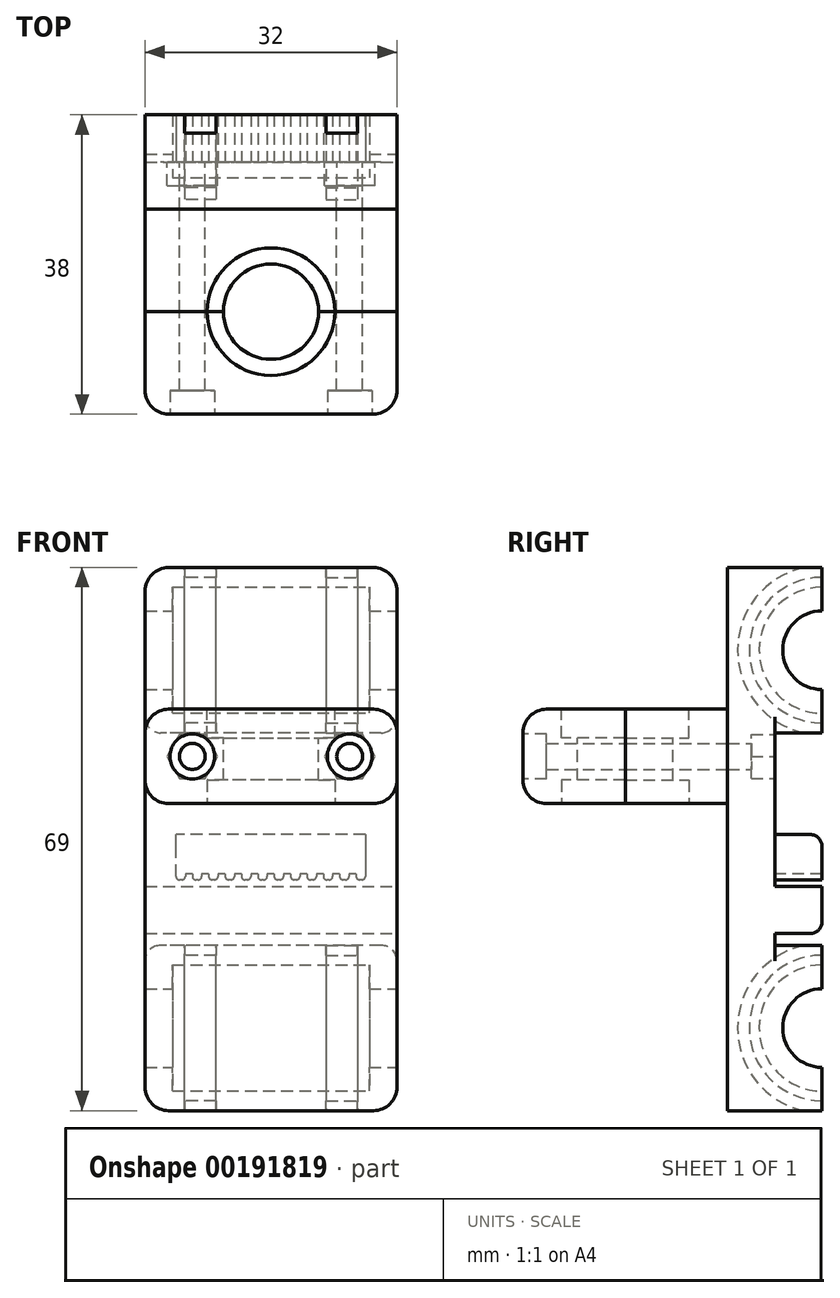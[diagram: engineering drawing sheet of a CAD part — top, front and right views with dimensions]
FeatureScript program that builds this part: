
annotation { "Feature Type Name" : "Feature", "Feature Type Description" : "" }
export const myFeature = defineFeature(function(context is Context, id is Id, definition is map)
    precondition{}
    {
        {
            var Q0;
            Q0=qCreatedBy(makeId("Front.planeOp"),FACE);
            var sketch = newSketch(context, id + "F0", { "sketchPlane" : qUnion([Q0])});
            skLineSegment(sketch, "E0.bottom", {"start": v(-16, 34.5) * mm, "end": v(16, 34.5) * mm});
            skLineSegment(sketch, "E0.top", {"start": v(-16, -34.5) * mm, "end": v(16, -34.5) * mm});
            skLineSegment(sketch, "E0.left", {"start": v(-16, 34.5) * mm, "end": v(-16, -34.5) * mm});
            skLineSegment(sketch, "E0.right", {"start": v(16, 34.5) * mm, "end": v(16, -34.5) * mm});
            skPoint(sketch, "E0.middle", {"position": v(0, 0) * mm});
            skLineSegment(sketch, "E1.bottom", {"start": v(-30, 24) * mm, "end": v(30, 24) * mm, "construction": true});
            skLineSegment(sketch, "E1.top", {"start": v(-30, -24) * mm, "end": v(30, -24) * mm, "construction": true});
            skLineSegment(sketch, "E1.left", {"start": v(-30, 24) * mm, "end": v(-30, -24) * mm, "construction": true});
            skLineSegment(sketch, "E1.right", {"start": v(30, 24) * mm, "end": v(30, -24) * mm, "construction": true});
            skSolve(sketch);
        }
        {
            var Q0;
            Q0=makeQuery(id+"F0.imprint","IMPRINT",FACE,{"disambiguationData":[TD([[makeQuery(id+"F0.imprint","IMPRINT",EDGE,{"derivedFrom":sQuery(id+"F0.wireOp",EDGE,"E0.bottom")}),-1.0]])]});
            extrude(context, id + "F1", {"entities" : qUnion([Q0]), "depth" : 6 * mm});
        }
        {
            var Q0;
            Q0=makeQuery(id+"F0.imprint","IMPRINT",FACE,{"disambiguationData":[TD([[makeQuery(id+"F0.imprint","IMPRINT",EDGE,{"derivedFrom":sQuery(id+"F0.wireOp",EDGE,"E0.bottom")}),-1.0]])]});
            var sketch = newSketch(context, id + "F2", { "sketchPlane" : qUnion([Q0])});
            skLineSegment(sketch, "E2.bottom", {"start": v(16, 34.5) * mm, "end": v(-16, 34.5) * mm});
            skLineSegment(sketch, "E2.top", {"start": v(16, 13.5) * mm, "end": v(-16, 13.5) * mm});
            skLineSegment(sketch, "E2.left", {"start": v(16, 34.5) * mm, "end": v(16, 13.5) * mm});
            skLineSegment(sketch, "E2.right", {"start": v(-16, 34.5) * mm, "end": v(-16, 13.5) * mm});
            skPoint(sketch, "E2.middle", {"position": v(0, 24) * mm});
            skLineSegment(sketch, "E3.bottom", {"start": v(16, -13.5) * mm, "end": v(-16, -13.5) * mm});
            skLineSegment(sketch, "E3.top", {"start": v(16, -34.5) * mm, "end": v(-16, -34.5) * mm});
            skLineSegment(sketch, "E3.left", {"start": v(16, -13.5) * mm, "end": v(16, -34.5) * mm});
            skLineSegment(sketch, "E3.right", {"start": v(-16, -13.5) * mm, "end": v(-16, -34.5) * mm});
            skPoint(sketch, "E3.middle", {"position": v(0, -24) * mm});
            skSolve(sketch);
        }
        {
            var Q0;
            Q0=makeQuery(id+"F2.imprint","IMPRINT",FACE,{"disambiguationData":[TD([[makeQuery(id+"F2.imprint","IMPRINT",EDGE,{"derivedFrom":sQuery(id+"F2.wireOp",EDGE,"E2.bottom")}),-1.0]])]});
            var Q1;
            Q1=makeQuery(id+"F2.imprint","IMPRINT",FACE,{"disambiguationData":[TD([[makeQuery(id+"F2.imprint","IMPRINT",EDGE,{"derivedFrom":sQuery(id+"F2.wireOp",EDGE,"E3.bottom")}),1.0]])]});
            extrude(context, id + "F3", {"entities" : qUnion([Q0, Q1]), "operationType" : NewBodyOperationType.ADD, "oppositeDirection" : true, "depth" : 6 * mm});
        }
        {
            var Q0;
            Q0=makeQuery(id+"F3.boolean.opBoolean","MERGE",FACE,{"derivedFrom":[makeQuery(id+"F1.opExtrude","SWEPT_FACE",FACE,{"disambiguationData":[OSD([sQuery(id+"F0.wireOp",EDGE,"E0.right")])]}),makeQuery(id+"F3.opExtrude","SWEPT_FACE",FACE,{"disambiguationData":[OSD([sQuery(id+"F2.wireOp",EDGE,"E2.left")])]}),makeQuery(id+"F3.opExtrude","SWEPT_FACE",FACE,{"disambiguationData":[OSD([sQuery(id+"F2.wireOp",EDGE,"E3.left")])]})]});
            cPlane(context, id + "F4", {"entities" : qUnion([Q0]), "cplaneType" : CPlaneType.OFFSET, "offset" : 3.5 * mm, "oppositeDirection" : true, "width" : 150 * mm, "height" : 150 * mm});
        }
        {
            var Q0;
            Q0=qCreatedBy(id+"F4.planeOp",FACE);
            var sketch = newSketch(context, id + "F5", { "sketchPlane" : qUnion([Q0])});
            skCircle(sketch, "E4", {"center": v(6, 24) * mm, "radius": 8 * mm});
            skCircle(sketch, "E5", {"center": v(6, -24) * mm, "radius": 8 * mm});
            skSolve(sketch);
        }
        {
            var Q0;
            Q0=makeQuery(id+"F5.imprint","IMPRINT",FACE,{"disambiguationData":[TD([[makeQuery(id+"F5.imprint","IMPRINT",EDGE,{"derivedFrom":sQuery(id+"F5.wireOp",EDGE,"E4")}),1.0]])]});
            var Q1;
            Q1=makeQuery(id+"F5.imprint","IMPRINT",FACE,{"disambiguationData":[TD([[makeQuery(id+"F5.imprint","IMPRINT",EDGE,{"derivedFrom":sQuery(id+"F5.wireOp",EDGE,"E5")}),1.0]])]});
            extrude(context, id + "F6", {"entities" : qUnion([Q0, Q1]), "operationType" : NewBodyOperationType.REMOVE, "oppositeDirection" : true, "depth" : 25 * mm});
        }
        {
            var Q0;
            Q0=makeQuery(id+"F3.boolean.opBoolean","MERGE",FACE,{"derivedFrom":[makeQuery(id+"F1.opExtrude","SWEPT_FACE",FACE,{"disambiguationData":[OSD([sQuery(id+"F0.wireOp",EDGE,"E0.right")])]}),makeQuery(id+"F3.opExtrude","SWEPT_FACE",FACE,{"disambiguationData":[OSD([sQuery(id+"F2.wireOp",EDGE,"E2.left")])]}),makeQuery(id+"F3.opExtrude","SWEPT_FACE",FACE,{"disambiguationData":[OSD([sQuery(id+"F2.wireOp",EDGE,"E3.left")])]})]});
            var sketch = newSketch(context, id + "F7", { "sketchPlane" : qUnion([Q0])});
            skCircle(sketch, "E6", {"center": v(6, 24) * mm, "radius": 5 * mm});
            skCircle(sketch, "E7", {"center": v(6, -24) * mm, "radius": 5 * mm});
            skSolve(sketch);
        }
        {
            var Q0;
            {var subQ0=sQuery(id+"F7.wireOp",EDGE,"E6");var subQ1=makeQuery(id+"F3.opExtrude","CAP_EDGE",EDGE,{"disambiguationData":[OSD([sQuery(id+"F2.wireOp",EDGE,"E2.left")])],"isStart":false});var subQ2=makeQuery(id+"F7.imprint","INTERSECT",VERTEX,{"disambiguationData":[OD(0.0)],"derivedFrom":[subQ1,subQ0]});Q0=makeQuery(id+"F7.imprint","IMPRINT",FACE,{"disambiguationData":[TD([[makeQuery(id+"F7.imprint","IMPRINT",EDGE,{"disambiguationData":[TD([[subQ2,-1.0]])],"derivedFrom":subQ0}),1.0]])]});}
            var Q1;
            {var subQ0=sQuery(id+"F7.wireOp",EDGE,"E7");var subQ1=makeQuery(id+"F3.opExtrude","CAP_EDGE",EDGE,{"disambiguationData":[OSD([sQuery(id+"F2.wireOp",EDGE,"E3.left")])],"isStart":false});var subQ2=makeQuery(id+"F7.imprint","INTERSECT",VERTEX,{"disambiguationData":[OD(0.0)],"derivedFrom":[subQ1,subQ0]});Q1=makeQuery(id+"F7.imprint","IMPRINT",FACE,{"disambiguationData":[TD([[makeQuery(id+"F7.imprint","IMPRINT",EDGE,{"disambiguationData":[TD([[subQ2,1.0]])],"derivedFrom":subQ0}),1.0]])]});}
            var Q2;
            Q2=makeQuery(id+"F3.boolean.opBoolean","MERGE",FACE,{"derivedFrom":[makeQuery(id+"F1.opExtrude","SWEPT_FACE",FACE,{"disambiguationData":[OSD([sQuery(id+"F0.wireOp",EDGE,"E0.left")])]}),makeQuery(id+"F3.opExtrude","SWEPT_FACE",FACE,{"disambiguationData":[OSD([sQuery(id+"F2.wireOp",EDGE,"E2.right")])]}),makeQuery(id+"F3.opExtrude","SWEPT_FACE",FACE,{"disambiguationData":[OSD([sQuery(id+"F2.wireOp",EDGE,"E3.right")])]})]});
            extrude(context, id + "F8", {"entities" : qUnion([Q0, Q1]), "operationType" : NewBodyOperationType.REMOVE, "endBound" : BoundingType.UP_TO_SURFACE, "oppositeDirection" : true, "endBoundEntityFace" : qUnion([Q2]), "depth" : 25 * mm});
        }
        {
            var Q0;
            Q0=makeQuery(id+"F3.boolean.opBoolean","MERGE",FACE,{"derivedFrom":[makeQuery(id+"F1.opExtrude","SWEPT_FACE",FACE,{"disambiguationData":[OSD([sQuery(id+"F0.wireOp",EDGE,"E0.right")])]}),makeQuery(id+"F3.opExtrude","SWEPT_FACE",FACE,{"disambiguationData":[OSD([sQuery(id+"F2.wireOp",EDGE,"E2.left")])]}),makeQuery(id+"F3.opExtrude","SWEPT_FACE",FACE,{"disambiguationData":[OSD([sQuery(id+"F2.wireOp",EDGE,"E3.left")])]})]});
            cPlane(context, id + "F9", {"entities" : qUnion([Q0]), "cplaneType" : CPlaneType.OFFSET, "offset" : 5 * mm, "oppositeDirection" : true, "width" : 150 * mm, "height" : 150 * mm});
        }
        {
            var Q0;
            Q0=makeQuery(id+"F3.boolean.opBoolean","MERGE",FACE,{"derivedFrom":[makeQuery(id+"F1.opExtrude","SWEPT_FACE",FACE,{"disambiguationData":[OSD([sQuery(id+"F0.wireOp",EDGE,"E0.left")])]}),makeQuery(id+"F3.opExtrude","SWEPT_FACE",FACE,{"disambiguationData":[OSD([sQuery(id+"F2.wireOp",EDGE,"E2.right")])]}),makeQuery(id+"F3.opExtrude","SWEPT_FACE",FACE,{"disambiguationData":[OSD([sQuery(id+"F2.wireOp",EDGE,"E3.right")])]})]});
            cPlane(context, id + "F10", {"entities" : qUnion([Q0]), "cplaneType" : CPlaneType.OFFSET, "offset" : 5 * mm, "oppositeDirection" : true, "width" : 150 * mm, "height" : 150 * mm});
        }
        {
            var Q0;
            Q0=qCreatedBy(id+"F9.planeOp",FACE);
            var sketch = newSketch(context, id + "F11", { "sketchPlane" : qUnion([Q0])});
            skCircle(sketch, "E8", {"center": v(6, 24) * mm, "radius": 9.25 * mm});
            skCircle(sketch, "E9", {"center": v(6, 24) * mm, "radius": 10.75 * mm});
            skCircle(sketch, "E10", {"center": v(6, -24) * mm, "radius": 10.75 * mm});
            skCircle(sketch, "E11", {"center": v(6, -24) * mm, "radius": 9.25 * mm});
            skSolve(sketch);
        }
        {
            var Q0;
            Q0=makeQuery(id+"F11.imprint","IMPRINT",FACE,{"disambiguationData":[TD([[makeQuery(id+"F11.imprint","IMPRINT",EDGE,{"derivedFrom":sQuery(id+"F11.wireOp",EDGE,"E8")}),-1.0]])]});
            var Q1;
            Q1=makeQuery(id+"F11.imprint","IMPRINT",FACE,{"disambiguationData":[TD([[makeQuery(id+"F11.imprint","IMPRINT",EDGE,{"derivedFrom":sQuery(id+"F11.wireOp",EDGE,"E10")}),1.0]])]});
            extrude(context, id + "F12", {"entities" : qUnion([Q0, Q1]), "operationType" : NewBodyOperationType.REMOVE, "oppositeDirection" : true, "depth" : 4 * mm});
        }
        {
            var Q0;
            Q0=qCreatedBy(id+"F10.planeOp",FACE);
            var sketch = newSketch(context, id + "F13", { "sketchPlane" : qUnion([Q0])});
            skCircle(sketch, "E12", {"center": v(-6, 24) * mm, "radius": 10.75 * mm});
            skCircle(sketch, "E13", {"center": v(-6, 24) * mm, "radius": 9.25 * mm});
            skCircle(sketch, "E14", {"center": v(-6, -24) * mm, "radius": 10.75 * mm});
            skCircle(sketch, "E15", {"center": v(-6, -24) * mm, "radius": 9.25 * mm});
            skSolve(sketch);
        }
        {
            var Q0;
            Q0=makeQuery(id+"F13.imprint","IMPRINT",FACE,{"disambiguationData":[TD([[makeQuery(id+"F13.imprint","IMPRINT",EDGE,{"derivedFrom":sQuery(id+"F13.wireOp",EDGE,"E12")}),1.0]])]});
            var Q1;
            Q1=makeQuery(id+"F13.imprint","IMPRINT",FACE,{"disambiguationData":[TD([[makeQuery(id+"F13.imprint","IMPRINT",EDGE,{"derivedFrom":sQuery(id+"F13.wireOp",EDGE,"E14")}),1.0]])]});
            extrude(context, id + "F14", {"entities" : qUnion([Q0, Q1]), "operationType" : NewBodyOperationType.REMOVE, "oppositeDirection" : true, "depth" : 4 * mm});
        }
        {
            var Q0;
            Q0=makeQuery(id+"F3.opExtrude","SWEPT_EDGE",EDGE,{"disambiguationData":[OSD([sQuery(id+"F0.wireOp",EDGE,"E0.right"),sQuery(id+"F2.wireOp",EDGE,"E2.top"),sQuery(id+"F2.wireOp",EDGE,"E2.left")])]});
            var Q1;
            Q1=makeQuery(id+"F3.opExtrude","SWEPT_EDGE",EDGE,{"disambiguationData":[OSD([sQuery(id+"F0.wireOp",EDGE,"E0.left"),sQuery(id+"F2.wireOp",EDGE,"E2.top"),sQuery(id+"F2.wireOp",EDGE,"E2.right")])]});
            var Q2;
            Q2=makeQuery(id+"F3.opExtrude","SWEPT_EDGE",EDGE,{"disambiguationData":[OSD([sQuery(id+"F0.wireOp",EDGE,"E0.right"),sQuery(id+"F2.wireOp",EDGE,"E3.bottom"),sQuery(id+"F2.wireOp",EDGE,"E3.left")])]});
            var Q3;
            Q3=makeQuery(id+"F3.opExtrude","SWEPT_EDGE",EDGE,{"disambiguationData":[OSD([sQuery(id+"F0.wireOp",EDGE,"E0.left"),sQuery(id+"F2.wireOp",EDGE,"E3.bottom"),sQuery(id+"F2.wireOp",EDGE,"E3.right")])]});
            fillet(context, id + "F15", {"entities" : qUnion([Q0, Q1, Q2, Q3]), "radius" : 2 * mm, "tangentPropagation" : true, "allowEdgeOverflow" : false});
        }
        {
            var Q0;
            Q0=makeQuery(id+"F3.boolean.opBoolean","MERGE",EDGE,{"derivedFrom":[makeQuery(id+"F1.opExtrude","SWEPT_EDGE",EDGE,{"disambiguationData":[OSD([sQuery(id+"F0.wireOp",EDGE,"E0.top"),sQuery(id+"F0.wireOp",EDGE,"E0.right")])]}),makeQuery(id+"F3.opExtrude","SWEPT_EDGE",EDGE,{"disambiguationData":[OSD([sQuery(id+"F2.wireOp",EDGE,"E3.top"),sQuery(id+"F2.wireOp",EDGE,"E3.left")])]})]});
            var Q1;
            Q1=makeQuery(id+"F3.boolean.opBoolean","MERGE",EDGE,{"derivedFrom":[makeQuery(id+"F1.opExtrude","SWEPT_EDGE",EDGE,{"disambiguationData":[OSD([sQuery(id+"F0.wireOp",EDGE,"E0.top"),sQuery(id+"F0.wireOp",EDGE,"E0.left")])]}),makeQuery(id+"F3.opExtrude","SWEPT_EDGE",EDGE,{"disambiguationData":[OSD([sQuery(id+"F2.wireOp",EDGE,"E3.top"),sQuery(id+"F2.wireOp",EDGE,"E3.right")])]})]});
            var Q2;
            Q2=makeQuery(id+"F3.boolean.opBoolean","MERGE",EDGE,{"derivedFrom":[makeQuery(id+"F1.opExtrude","SWEPT_EDGE",EDGE,{"disambiguationData":[OSD([sQuery(id+"F0.wireOp",EDGE,"E0.bottom"),sQuery(id+"F0.wireOp",EDGE,"E0.right")])]}),makeQuery(id+"F3.opExtrude","SWEPT_EDGE",EDGE,{"disambiguationData":[OSD([sQuery(id+"F2.wireOp",EDGE,"E2.bottom"),sQuery(id+"F2.wireOp",EDGE,"E2.left")])]})]});
            var Q3;
            Q3=makeQuery(id+"F3.boolean.opBoolean","MERGE",EDGE,{"derivedFrom":[makeQuery(id+"F1.opExtrude","SWEPT_EDGE",EDGE,{"disambiguationData":[OSD([sQuery(id+"F0.wireOp",EDGE,"E0.bottom"),sQuery(id+"F0.wireOp",EDGE,"E0.left")])]}),makeQuery(id+"F3.opExtrude","SWEPT_EDGE",EDGE,{"disambiguationData":[OSD([sQuery(id+"F2.wireOp",EDGE,"E2.bottom"),sQuery(id+"F2.wireOp",EDGE,"E2.right")])]})]});
            fillet(context, id + "F16", {"entities" : qUnion([Q0, Q1, Q2, Q3]), "radius" : 3 * mm, "tangentPropagation" : true, "allowEdgeOverflow" : false});
        }
        {
            var Q0;
            Q0=makeQuery(id+"F1.opExtrude","CAP_FACE",FACE,{"disambiguationData":[OSD([sQuery(id+"F0.wireOp",EDGE,"E0.bottom"),sQuery(id+"F0.wireOp",EDGE,"E0.top"),sQuery(id+"F0.wireOp",EDGE,"E0.left"),sQuery(id+"F0.wireOp",EDGE,"E0.right")])],"isStart":true});
            var sketch = newSketch(context, id + "F17", { "sketchPlane" : qUnion([Q0])});
            skCircle(sketch, "E16", {"center": v(-10, 10.5) * mm, "radius": 1.65 * mm});
            skCircle(sketch, "E17", {"center": v(10, 10.5) * mm, "radius": 1.65 * mm});
            skCircle(sketch, "E18.cCircle", {"center": v(-10, 10.5) * mm, "radius": 2.8 * mm, "construction": true});
            skLineSegment(sketch, "E18.0", {"start": v(-13.23, 10.5) * mm, "end": v(-11.62, 13.3) * mm});
            skLineSegment(sketch, "E18.1", {"start": v(-11.62, 13.3) * mm, "end": v(-8.38, 13.3) * mm});
            skLineSegment(sketch, "E18.2", {"start": v(-8.38, 13.3) * mm, "end": v(-6.77, 10.5) * mm});
            skLineSegment(sketch, "E18.3", {"start": v(-6.77, 10.5) * mm, "end": v(-8.38, 7.7) * mm});
            skLineSegment(sketch, "E18.4", {"start": v(-8.38, 7.7) * mm, "end": v(-11.62, 7.7) * mm});
            skLineSegment(sketch, "E18.5", {"start": v(-11.62, 7.7) * mm, "end": v(-13.23, 10.5) * mm});
            skPoint(sketch, "E18.0.midPoint", {"position": v(-12.42, 11.9) * mm});
            skCircle(sketch, "E19.cCircle", {"center": v(10, 10.5) * mm, "radius": 2.8 * mm, "construction": true});
            skLineSegment(sketch, "E19.0", {"start": v(6.77, 10.5) * mm, "end": v(8.38, 13.3) * mm});
            skLineSegment(sketch, "E19.1", {"start": v(8.38, 13.3) * mm, "end": v(11.62, 13.3) * mm});
            skLineSegment(sketch, "E19.2", {"start": v(11.62, 13.3) * mm, "end": v(13.23, 10.5) * mm});
            skLineSegment(sketch, "E19.3", {"start": v(13.23, 10.5) * mm, "end": v(11.62, 7.7) * mm});
            skLineSegment(sketch, "E19.4", {"start": v(11.62, 7.7) * mm, "end": v(8.38, 7.7) * mm});
            skLineSegment(sketch, "E19.5", {"start": v(8.38, 7.7) * mm, "end": v(6.77, 10.5) * mm});
            skPoint(sketch, "E19.0.midPoint", {"position": v(7.58, 11.9) * mm});
            skSolve(sketch);
        }
        {
            var Q0;
            Q0=makeQuery(id+"F17.imprint","IMPRINT",FACE,{"disambiguationData":[TD([[makeQuery(id+"F17.imprint","IMPRINT",EDGE,{"derivedFrom":sQuery(id+"F17.wireOp",EDGE,"E16")}),1.0]])]});
            var Q1;
            Q1=makeQuery(id+"F17.imprint","IMPRINT",FACE,{"disambiguationData":[TD([[makeQuery(id+"F17.imprint","IMPRINT",EDGE,{"derivedFrom":sQuery(id+"F17.wireOp",EDGE,"E17")}),1.0]])]});
            extrude(context, id + "F18", {"entities" : qUnion([Q0, Q1]), "operationType" : NewBodyOperationType.REMOVE, "endBound" : BoundingType.THROUGH_ALL, "oppositeDirection" : true, "depth" : 25 * mm});
        }
        {
            var Q0;
            Q0=makeQuery(id+"F17.imprint","IMPRINT",FACE,{"disambiguationData":[TD([[makeQuery(id+"F17.imprint","IMPRINT",EDGE,{"derivedFrom":sQuery(id+"F17.wireOp",EDGE,"E16")}),-1.0]])]});
            var Q1;
            Q1=makeQuery(id+"F17.imprint","IMPRINT",FACE,{"disambiguationData":[TD([[makeQuery(id+"F17.imprint","IMPRINT",EDGE,{"derivedFrom":sQuery(id+"F17.wireOp",EDGE,"E17")}),-1.0]])]});
            extrude(context, id + "F19", {"entities" : qUnion([Q0, Q1]), "operationType" : NewBodyOperationType.REMOVE, "oppositeDirection" : true, "depth" : 3 * mm});
        }
        {
            var Q0;
            Q0=makeQuery(id+"F1.opExtrude","CAP_FACE",FACE,{"disambiguationData":[OSD([sQuery(id+"F0.wireOp",EDGE,"E0.bottom"),sQuery(id+"F0.wireOp",EDGE,"E0.top"),sQuery(id+"F0.wireOp",EDGE,"E0.left"),sQuery(id+"F0.wireOp",EDGE,"E0.right")])],"isStart":false});
            var sketch = newSketch(context, id + "F20", { "sketchPlane" : qUnion([Q0])});
            skLineSegment(sketch, "E20.bottom", {"start": v(-16, 16.5) * mm, "end": v(16, 16.5) * mm});
            skLineSegment(sketch, "E20.top", {"start": v(-16, 4.5) * mm, "end": v(16, 4.5) * mm});
            skLineSegment(sketch, "E20.left", {"start": v(-16, 16.5) * mm, "end": v(-16, 4.5) * mm});
            skLineSegment(sketch, "E20.right", {"start": v(16, 16.5) * mm, "end": v(16, 4.5) * mm});
            skSolve(sketch);
        }
        {
            var Q0;
            Q0=makeQuery(id+"F20.imprint","IMPRINT",FACE,{"disambiguationData":[TD([[makeQuery(id+"F20.imprint","IMPRINT",EDGE,{"derivedFrom":sQuery(id+"F20.wireOp",EDGE,"E20.bottom")}),-1.0]])]});
            extrude(context, id + "F21", {"entities" : qUnion([Q0]), "depth" : (26 / 2) * mm});
        }
        {
            var Q0;
            Q0=makeQuery(id+"F21.opExtrude","CAP_FACE",FACE,{"disambiguationData":[OSD([sQuery(id+"F0.wireOp",EDGE,"E0.bottom"),sQuery(id+"F0.wireOp",EDGE,"E0.top"),sQuery(id+"F0.wireOp",EDGE,"E0.left"),sQuery(id+"F0.wireOp",EDGE,"E0.right"),sQuery(id+"F17.wireOp",EDGE,"E16"),sQuery(id+"F17.wireOp",EDGE,"E17"),sQuery(id+"F20.wireOp",EDGE,"E20.bottom"),sQuery(id+"F20.wireOp",EDGE,"E20.top"),sQuery(id+"F20.wireOp",EDGE,"E20.left"),sQuery(id+"F20.wireOp",EDGE,"E20.right")])],"isStart":false});
            extrude(context, id + "F22", {"entities" : qUnion([Q0]), "depth" : (26 / 2) * mm});
        }
        {
            var Q0;
            Q0=makeQuery(id+"F22.opExtrude","CAP_EDGE",EDGE,{"disambiguationData":[OSD([sQuery(id+"F20.wireOp",EDGE,"E20.left")])],"isStart":false});
            var Q1;
            Q1=makeQuery(id+"F22.opExtrude","CAP_EDGE",EDGE,{"disambiguationData":[OSD([sQuery(id+"F20.wireOp",EDGE,"E20.right")])],"isStart":false});
            var Q2;
            Q2=makeQuery(id+"F22.opExtrude","SWEPT_EDGE",EDGE,{"disambiguationData":[OSD([sQuery(id+"F0.wireOp",EDGE,"E0.right"),sQuery(id+"F20.wireOp",EDGE,"E20.bottom"),sQuery(id+"F20.wireOp",EDGE,"E20.right")])]});
            var Q3;
            Q3=makeQuery(id+"F21.opExtrude","SWEPT_EDGE",EDGE,{"disambiguationData":[OSD([sQuery(id+"F0.wireOp",EDGE,"E0.right"),sQuery(id+"F20.wireOp",EDGE,"E20.bottom"),sQuery(id+"F20.wireOp",EDGE,"E20.right")])]});
            var Q4;
            Q4=makeQuery(id+"F21.opExtrude","SWEPT_EDGE",EDGE,{"disambiguationData":[OSD([sQuery(id+"F0.wireOp",EDGE,"E0.right"),sQuery(id+"F20.wireOp",EDGE,"E20.top"),sQuery(id+"F20.wireOp",EDGE,"E20.right")])]});
            var Q5;
            Q5=makeQuery(id+"F22.opExtrude","SWEPT_EDGE",EDGE,{"disambiguationData":[OSD([sQuery(id+"F0.wireOp",EDGE,"E0.right"),sQuery(id+"F20.wireOp",EDGE,"E20.top"),sQuery(id+"F20.wireOp",EDGE,"E20.right")])]});
            var Q6;
            Q6=makeQuery(id+"F21.opExtrude","SWEPT_EDGE",EDGE,{"disambiguationData":[OSD([sQuery(id+"F0.wireOp",EDGE,"E0.left"),sQuery(id+"F20.wireOp",EDGE,"E20.top"),sQuery(id+"F20.wireOp",EDGE,"E20.left")])]});
            var Q7;
            Q7=makeQuery(id+"F22.opExtrude","SWEPT_EDGE",EDGE,{"disambiguationData":[OSD([sQuery(id+"F0.wireOp",EDGE,"E0.left"),sQuery(id+"F20.wireOp",EDGE,"E20.top"),sQuery(id+"F20.wireOp",EDGE,"E20.left")])]});
            var Q8;
            Q8=makeQuery(id+"F22.opExtrude","CAP_EDGE",EDGE,{"disambiguationData":[OSD([sQuery(id+"F20.wireOp",EDGE,"E20.top")])],"isStart":false});
            var Q9;
            Q9=makeQuery(id+"F22.opExtrude","CAP_EDGE",EDGE,{"disambiguationData":[OSD([sQuery(id+"F20.wireOp",EDGE,"E20.bottom")])],"isStart":false});
            var Q10;
            Q10=makeQuery(id+"F22.opExtrude","SWEPT_EDGE",EDGE,{"disambiguationData":[OSD([sQuery(id+"F0.wireOp",EDGE,"E0.left"),sQuery(id+"F20.wireOp",EDGE,"E20.bottom"),sQuery(id+"F20.wireOp",EDGE,"E20.left")])]});
            var Q11;
            Q11=makeQuery(id+"F21.opExtrude","SWEPT_EDGE",EDGE,{"disambiguationData":[OSD([sQuery(id+"F0.wireOp",EDGE,"E0.left"),sQuery(id+"F20.wireOp",EDGE,"E20.bottom"),sQuery(id+"F20.wireOp",EDGE,"E20.left")])]});
            fillet(context, id + "F23", {"entities" : qUnion([Q0, Q1, Q2, Q3, Q4, Q5, Q6, Q7, Q8, Q9, Q10, Q11]), "radius" : 3 * mm, "tangentPropagation" : true, "allowEdgeOverflow" : false});
        }
        {
            var Q0;
            Q0=makeQuery(id+"F21.opExtrude","SWEPT_FACE",FACE,{"disambiguationData":[OSD([sQuery(id+"F20.wireOp",EDGE,"E20.bottom")])]});
            var sketch = newSketch(context, id + "F24", { "sketchPlane" : qUnion([Q0])});
            skCircle(sketch, "E21", {"center": v(0, -19) * mm, "radius": 8.1 * mm});
            skSolve(sketch);
        }
        {
            var Q0;
            {var subQ0=sQuery(id+"F24.wireOp",EDGE,"E21");var subQ1=makeQuery(id+"F21.opExtrude","CAP_EDGE",EDGE,{"disambiguationData":[OSD([sQuery(id+"F20.wireOp",EDGE,"E20.bottom")])],"isStart":false});var subQ2=makeQuery(id+"F24.imprint","INTERSECT",VERTEX,{"disambiguationData":[OD(0.0)],"derivedFrom":[subQ1,subQ0]});Q0=makeQuery(id+"F24.imprint","IMPRINT",FACE,{"disambiguationData":[TD([[makeQuery(id+"F24.imprint","IMPRINT",EDGE,{"disambiguationData":[TD([[subQ2,1.0]])],"derivedFrom":subQ0}),1.0]])]});}
            var Q1;
            {var subQ0=sQuery(id+"F24.wireOp",EDGE,"E21");var subQ1=makeQuery(id+"F21.opExtrude","CAP_EDGE",EDGE,{"disambiguationData":[OSD([sQuery(id+"F20.wireOp",EDGE,"E20.bottom")])],"isStart":false});var subQ2=makeQuery(id+"F24.imprint","INTERSECT",VERTEX,{"disambiguationData":[OD(0.0)],"derivedFrom":[subQ1,subQ0]});Q1=makeQuery(id+"F24.imprint","IMPRINT",FACE,{"disambiguationData":[TD([[makeQuery(id+"F24.imprint","IMPRINT",EDGE,{"disambiguationData":[TD([[subQ2,-1.0]])],"derivedFrom":subQ0}),1.0]])]});}
            extrude(context, id + "F25", {"entities" : qUnion([Q0, Q1]), "operationType" : NewBodyOperationType.REMOVE, "oppositeDirection" : true, "depth" : 3.65 * mm});
        }
        {
            var Q0;
            Q0=makeQuery(id+"F21.opExtrude","SWEPT_FACE",FACE,{"disambiguationData":[OSD([sQuery(id+"F20.wireOp",EDGE,"E20.top")])]});
            var sketch = newSketch(context, id + "F26", { "sketchPlane" : qUnion([Q0])});
            skCircle(sketch, "E22", {"center": v(0, 19) * mm, "radius": 8.1 * mm});
            skSolve(sketch);
        }
        {
            var Q0;
            {var subQ0=sQuery(id+"F26.wireOp",EDGE,"E22");var subQ1=makeQuery(id+"F21.opExtrude","CAP_EDGE",EDGE,{"disambiguationData":[OSD([sQuery(id+"F20.wireOp",EDGE,"E20.top")])],"isStart":false});var subQ2=makeQuery(id+"F26.imprint","INTERSECT",VERTEX,{"disambiguationData":[OD(0.0)],"derivedFrom":[subQ1,subQ0]});Q0=makeQuery(id+"F26.imprint","IMPRINT",FACE,{"disambiguationData":[TD([[makeQuery(id+"F26.imprint","IMPRINT",EDGE,{"disambiguationData":[TD([[subQ2,1.0]])],"derivedFrom":subQ0}),1.0]])]});}
            var Q1;
            {var subQ0=sQuery(id+"F26.wireOp",EDGE,"E22");var subQ1=makeQuery(id+"F21.opExtrude","CAP_EDGE",EDGE,{"disambiguationData":[OSD([sQuery(id+"F20.wireOp",EDGE,"E20.top")])],"isStart":false});var subQ2=makeQuery(id+"F26.imprint","INTERSECT",VERTEX,{"disambiguationData":[OD(0.0)],"derivedFrom":[subQ1,subQ0]});Q1=makeQuery(id+"F26.imprint","IMPRINT",FACE,{"disambiguationData":[TD([[makeQuery(id+"F26.imprint","IMPRINT",EDGE,{"disambiguationData":[TD([[subQ2,-1.0]])],"derivedFrom":subQ0}),1.0]])]});}
            extrude(context, id + "F27", {"entities" : qUnion([Q0, Q1]), "operationType" : NewBodyOperationType.REMOVE, "oppositeDirection" : true, "depth" : 3 * mm});
        }
        {
            var Q0;
            {var subQ0=sQuery(id+"F24.wireOp",EDGE,"E21");Q0=makeQuery(id+"F25.boolean.opBoolean","COPY",FACE,{"disambiguationData":[TD([makeQuery(id+"F21.opExtrude","CAP_FACE",FACE,{"disambiguationData":[OSD([sQuery(id+"F0.wireOp",EDGE,"E0.bottom"),sQuery(id+"F0.wireOp",EDGE,"E0.top"),sQuery(id+"F0.wireOp",EDGE,"E0.left"),sQuery(id+"F0.wireOp",EDGE,"E0.right"),sQuery(id+"F17.wireOp",EDGE,"E16"),sQuery(id+"F17.wireOp",EDGE,"E17"),sQuery(id+"F20.wireOp",EDGE,"E20.bottom"),sQuery(id+"F20.wireOp",EDGE,"E20.top"),sQuery(id+"F20.wireOp",EDGE,"E20.left"),sQuery(id+"F20.wireOp",EDGE,"E20.right")])],"isStart":false})])],"derivedFrom":makeQuery(id+"F25.opExtrude","CAP_FACE",FACE,{"disambiguationData":[OSD([subQ0])],"isStart":false})});}
            var sketch = newSketch(context, id + "F28", { "sketchPlane" : qUnion([Q0])});
            skCircle(sketch, "E23", {"center": v(0, -19) * mm, "radius": 6.05 * mm});
            skSolve(sketch);
        }
        {
            var Q0;
            {var subQ0=sQuery(id+"F28.wireOp",EDGE,"E23");var subQ1=makeQuery(id+"F25.boolean.opBoolean","INTERSECT",EDGE,{"derivedFrom":[makeQuery(id+"F21.opExtrude","CAP_FACE",FACE,{"disambiguationData":[OSD([sQuery(id+"F0.wireOp",EDGE,"E0.bottom"),sQuery(id+"F0.wireOp",EDGE,"E0.top"),sQuery(id+"F0.wireOp",EDGE,"E0.left"),sQuery(id+"F0.wireOp",EDGE,"E0.right"),sQuery(id+"F17.wireOp",EDGE,"E16"),sQuery(id+"F17.wireOp",EDGE,"E17"),sQuery(id+"F20.wireOp",EDGE,"E20.bottom"),sQuery(id+"F20.wireOp",EDGE,"E20.top"),sQuery(id+"F20.wireOp",EDGE,"E20.left"),sQuery(id+"F20.wireOp",EDGE,"E20.right")])],"isStart":false}),makeQuery(id+"F25.opExtrude","CAP_FACE",FACE,{"disambiguationData":[OSD([sQuery(id+"F24.wireOp",EDGE,"E21")])],"isStart":false})]});var subQ2=makeQuery(id+"F28.imprint","INTERSECT",VERTEX,{"disambiguationData":[OD(0.0)],"derivedFrom":[subQ1,subQ0]});Q0=makeQuery(id+"F28.imprint","IMPRINT",FACE,{"disambiguationData":[TD([[makeQuery(id+"F28.imprint","IMPRINT",EDGE,{"disambiguationData":[TD([[subQ2,1.0]])],"derivedFrom":subQ0}),1.0]])]});}
            var Q1;
            {var subQ0=sQuery(id+"F28.wireOp",EDGE,"E23");var subQ1=makeQuery(id+"F25.boolean.opBoolean","INTERSECT",EDGE,{"derivedFrom":[makeQuery(id+"F21.opExtrude","CAP_FACE",FACE,{"disambiguationData":[OSD([sQuery(id+"F0.wireOp",EDGE,"E0.bottom"),sQuery(id+"F0.wireOp",EDGE,"E0.top"),sQuery(id+"F0.wireOp",EDGE,"E0.left"),sQuery(id+"F0.wireOp",EDGE,"E0.right"),sQuery(id+"F17.wireOp",EDGE,"E16"),sQuery(id+"F17.wireOp",EDGE,"E17"),sQuery(id+"F20.wireOp",EDGE,"E20.bottom"),sQuery(id+"F20.wireOp",EDGE,"E20.top"),sQuery(id+"F20.wireOp",EDGE,"E20.left"),sQuery(id+"F20.wireOp",EDGE,"E20.right")])],"isStart":false}),makeQuery(id+"F25.opExtrude","CAP_FACE",FACE,{"disambiguationData":[OSD([sQuery(id+"F24.wireOp",EDGE,"E21")])],"isStart":false})]});var subQ2=makeQuery(id+"F28.imprint","INTERSECT",VERTEX,{"disambiguationData":[OD(0.0)],"derivedFrom":[subQ1,subQ0]});Q1=makeQuery(id+"F28.imprint","IMPRINT",FACE,{"disambiguationData":[TD([[makeQuery(id+"F28.imprint","IMPRINT",EDGE,{"disambiguationData":[TD([[subQ2,-1.0]])],"derivedFrom":subQ0}),1.0]])]});}
            extrude(context, id + "F29", {"entities" : qUnion([Q0, Q1]), "operationType" : NewBodyOperationType.REMOVE, "oppositeDirection" : true, "depth" : 25 * mm});
        }
        {
            var Q0;
            Q0=makeQuery(id+"F22.opExtrude","CAP_FACE",FACE,{"disambiguationData":[OSD([sQuery(id+"F0.wireOp",EDGE,"E0.bottom"),sQuery(id+"F0.wireOp",EDGE,"E0.top"),sQuery(id+"F0.wireOp",EDGE,"E0.left"),sQuery(id+"F0.wireOp",EDGE,"E0.right"),sQuery(id+"F17.wireOp",EDGE,"E16"),sQuery(id+"F17.wireOp",EDGE,"E17"),sQuery(id+"F20.wireOp",EDGE,"E20.bottom"),sQuery(id+"F20.wireOp",EDGE,"E20.top"),sQuery(id+"F20.wireOp",EDGE,"E20.left"),sQuery(id+"F20.wireOp",EDGE,"E20.right")])],"isStart":false});
            var sketch = newSketch(context, id + "F30", { "sketchPlane" : qUnion([Q0])});
            skCircle(sketch, "E24", {"center": v(-10, 10.5) * mm, "radius": 2.85 * mm});
            skCircle(sketch, "E25", {"center": v(10, 10.5) * mm, "radius": 2.85 * mm});
            skSolve(sketch);
        }
        {
            var Q0;
            Q0 = qSketchRegion(id + "F30", true);
            extrude(context, id + "F31", {"entities" : qUnion([Q0]), "operationType" : NewBodyOperationType.REMOVE, "oppositeDirection" : true, "depth" : 3 * mm});
        }
        {
            var Q0;
            Q0=makeQuery(id+"F0.imprint","IMPRINT",FACE,{"disambiguationData":[TD([[makeQuery(id+"F0.imprint","IMPRINT",EDGE,{"derivedFrom":sQuery(id+"F0.wireOp",EDGE,"E0.bottom")}),-1.0]])]});
            var sketch = newSketch(context, id + "F32", { "sketchPlane" : qUnion([Q0])});
            skLineSegment(sketch, "E26.bottom", {"start": v(-16, -12) * mm, "end": v(16, -12) * mm});
            skLineSegment(sketch, "E26.top", {"start": v(-16, -6) * mm, "end": v(16, -6) * mm});
            skLineSegment(sketch, "E26.left", {"start": v(-16, -12) * mm, "end": v(-16, -6) * mm});
            skLineSegment(sketch, "E26.right", {"start": v(16, -12) * mm, "end": v(16, -6) * mm});
            skLineSegment(sketch, "E27.bottom", {"start": v(12, 0.58) * mm, "end": v(-12, 0.58) * mm});
            skLineSegment(sketch, "E27.top", {"start": v(12, -4.42) * mm, "end": v(-12, -4.42) * mm});
            skLineSegment(sketch, "E27.left", {"start": v(12, 0.58) * mm, "end": v(12, -4.42) * mm});
            skLineSegment(sketch, "E27.right", {"start": v(-12, 0.58) * mm, "end": v(-12, -4.42) * mm});
            skLineSegment(sketch, "E28", {"start": v(7.4, -5.17) * mm, "end": v(7.1, -5.17) * mm});
            skLineSegment(sketch, "E29.bottom", {"start": v(12, -4.42) * mm, "end": v(10.8, -4.42) * mm, "construction": true});
            skLineSegment(sketch, "E29.top", {"start": v(11.55, -5.17) * mm, "end": v(11.25, -5.17) * mm});
            skLineSegment(sketch, "E29.left", {"start": v(12, -4.42) * mm, "end": v(12, -4.72) * mm});
            skLineSegment(sketch, "E29.right", {"start": v(10.8, -4.42) * mm, "end": v(10.8, -4.72) * mm});
            skLineSegment(sketch, "E30.bottom", {"start": v(9.92, -4.42) * mm, "end": v(8.72, -4.42) * mm, "construction": true});
            skLineSegment(sketch, "E30.top", {"start": v(9.92, -5.17) * mm, "end": v(8.72, -5.17) * mm});
            skLineSegment(sketch, "E30.left", {"start": v(9.92, -4.42) * mm, "end": v(9.92, -4.72) * mm});
            skLineSegment(sketch, "E30.right", {"start": v(8.72, -4.42) * mm, "end": v(8.72, -4.72) * mm});
            skLineSegment(sketch, "E31.1.0.0", {"start": v(7.84, -4.42) * mm, "end": v(7.84, -4.72) * mm});
            skLineSegment(sketch, "E31.1.0.1", {"start": v(6.64, -4.42) * mm, "end": v(6.64, -4.72) * mm});
            skLineSegment(sketch, "E31.2.0.0", {"start": v(5.76, -4.42) * mm, "end": v(5.76, -4.72) * mm});
            skLineSegment(sketch, "E31.2.0.1", {"start": v(4.56, -4.42) * mm, "end": v(4.56, -4.72) * mm});
            skLineSegment(sketch, "E31.3.0.0", {"start": v(3.68, -4.42) * mm, "end": v(3.68, -4.72) * mm});
            skLineSegment(sketch, "E31.3.0.1", {"start": v(2.48, -4.42) * mm, "end": v(2.48, -4.72) * mm});
            skLineSegment(sketch, "E31.4.0.0", {"start": v(1.6, -4.42) * mm, "end": v(1.6, -4.72) * mm});
            skLineSegment(sketch, "E31.4.0.1", {"start": v(0.4, -4.42) * mm, "end": v(0.4, -4.72) * mm});
            skLineSegment(sketch, "E31.5.0.0", {"start": v(-0.48, -4.42) * mm, "end": v(-0.48, -4.72) * mm});
            skLineSegment(sketch, "E31.5.0.1", {"start": v(-1.68, -4.42) * mm, "end": v(-1.68, -4.72) * mm});
            skLineSegment(sketch, "E31.6.0.0", {"start": v(-2.56, -4.42) * mm, "end": v(-2.56, -4.72) * mm});
            skLineSegment(sketch, "E31.6.0.1", {"start": v(-3.76, -4.42) * mm, "end": v(-3.76, -4.72) * mm});
            skLineSegment(sketch, "E31.7.0.0", {"start": v(-4.64, -4.42) * mm, "end": v(-4.64, -4.72) * mm});
            skLineSegment(sketch, "E31.7.0.1", {"start": v(-5.84, -4.42) * mm, "end": v(-5.84, -4.72) * mm});
            skLineSegment(sketch, "E31.8.0.0", {"start": v(-6.72, -4.42) * mm, "end": v(-6.72, -4.72) * mm});
            skLineSegment(sketch, "E31.8.0.1", {"start": v(-7.92, -4.42) * mm, "end": v(-7.92, -4.72) * mm});
            skLineSegment(sketch, "E31.9.0.0", {"start": v(-8.8, -4.42) * mm, "end": v(-8.8, -4.72) * mm});
            skLineSegment(sketch, "E31.9.0.1", {"start": v(-10, -4.42) * mm, "end": v(-10, -4.72) * mm});
            skLineSegment(sketch, "E31.direction1", {"start": v(9.47, -5.17) * mm, "end": v(9.17, -5.17) * mm, "construction": true});
            skPoint(sketch, "E32.visualSharp", {"position": v(12, -5.17) * mm});
            skArc(sketch, "E32.filletArc", {"start": v(11.55, -5.17) * mm, "mid": v(11.87, -5.04) * mm, "end": v(12, -4.72) * mm});
            skPoint(sketch, "E33.visualSharp", {"position": v(10.8, -5.17) * mm});
            skArc(sketch, "E33.filletArc", {"start": v(10.8, -4.72) * mm, "mid": v(10.93, -5.04) * mm, "end": v(11.25, -5.17) * mm});
            skPoint(sketch, "E34.visualSharp", {"position": v(9.92, -5.17) * mm});
            skArc(sketch, "E34.filletArc", {"start": v(9.47, -5.17) * mm, "mid": v(9.79, -5.04) * mm, "end": v(9.92, -4.72) * mm});
            skPoint(sketch, "E35.newPointA", {"position": v(7.84, -5.17) * mm});
            skPoint(sketch, "E35.newPointB", {"position": v(8.72, -5.17) * mm});
            skArc(sketch, "E35.filletArc", {"start": v(8.72, -4.72) * mm, "mid": v(8.85, -5.04) * mm, "end": v(9.17, -5.17) * mm});
            skPoint(sketch, "E36.newPointB", {"position": v(16, -5.17) * mm});
            skArc(sketch, "E36.filletArc", {"start": v(7.4, -5.17) * mm, "mid": v(7.7, -5.04) * mm, "end": v(7.84, -4.72) * mm});
            skPoint(sketch, "E37.newPointA", {"position": v(-16, -5.17) * mm});
            skPoint(sketch, "E37.newPointB", {"position": v(6.64, -5.17) * mm});
            skArc(sketch, "E37.filletArc", {"start": v(6.64, -4.72) * mm, "mid": v(6.77, -5.04) * mm, "end": v(7.1, -5.17) * mm});
            skLineSegment(sketch, "E38", {"start": v(5.31, -5.17) * mm, "end": v(5.01, -5.17) * mm});
            skLineSegment(sketch, "E39", {"start": v(3.23, -5.17) * mm, "end": v(2.93, -5.17) * mm});
            skLineSegment(sketch, "E40", {"start": v(1.15, -5.17) * mm, "end": v(0.85, -5.17) * mm});
            skLineSegment(sketch, "E41", {"start": v(-0.93, -5.17) * mm, "end": v(-1.23, -5.17) * mm});
            skLineSegment(sketch, "E42", {"start": v(-3, -5.17) * mm, "end": v(-3.3, -5.17) * mm});
            skLineSegment(sketch, "E43", {"start": v(-5.09, -5.17) * mm, "end": v(-5.39, -5.17) * mm});
            skLineSegment(sketch, "E44", {"start": v(-7.17, -5.17) * mm, "end": v(-7.47, -5.17) * mm});
            skLineSegment(sketch, "E45", {"start": v(-9.25, -5.17) * mm, "end": v(-9.55, -5.17) * mm});
            skPoint(sketch, "E46.visualSharp", {"position": v(5.76, -5.17) * mm});
            skArc(sketch, "E46.filletArc", {"start": v(5.31, -5.17) * mm, "mid": v(5.63, -5.04) * mm, "end": v(5.76, -4.72) * mm});
            skPoint(sketch, "E47.visualSharp", {"position": v(4.56, -5.17) * mm});
            skArc(sketch, "E47.filletArc", {"start": v(4.56, -4.72) * mm, "mid": v(4.7, -5.04) * mm, "end": v(5.01, -5.17) * mm});
            skPoint(sketch, "E48.visualSharp", {"position": v(3.68, -5.17) * mm});
            skArc(sketch, "E48.filletArc", {"start": v(3.23, -5.17) * mm, "mid": v(3.55, -5.04) * mm, "end": v(3.68, -4.72) * mm});
            skPoint(sketch, "E49.visualSharp", {"position": v(2.48, -5.17) * mm});
            skArc(sketch, "E49.filletArc", {"start": v(2.48, -4.72) * mm, "mid": v(2.61, -5.04) * mm, "end": v(2.93, -5.17) * mm});
            skPoint(sketch, "E50.visualSharp", {"position": v(1.6, -5.17) * mm});
            skArc(sketch, "E50.filletArc", {"start": v(1.15, -5.17) * mm, "mid": v(1.47, -5.04) * mm, "end": v(1.6, -4.72) * mm});
            skPoint(sketch, "E51.visualSharp", {"position": v(0.4, -5.17) * mm});
            skArc(sketch, "E51.filletArc", {"start": v(0.4, -4.72) * mm, "mid": v(0.53, -5.04) * mm, "end": v(0.85, -5.17) * mm});
            skPoint(sketch, "E52.visualSharp", {"position": v(-0.48, -5.17) * mm});
            skArc(sketch, "E52.filletArc", {"start": v(-0.93, -5.17) * mm, "mid": v(-0.61, -5.04) * mm, "end": v(-0.48, -4.72) * mm});
            skPoint(sketch, "E53.visualSharp", {"position": v(-1.68, -5.17) * mm});
            skArc(sketch, "E53.filletArc", {"start": v(-1.68, -4.72) * mm, "mid": v(-1.55, -5.04) * mm, "end": v(-1.23, -5.17) * mm});
            skPoint(sketch, "E54.visualSharp", {"position": v(-2.56, -5.17) * mm});
            skArc(sketch, "E54.filletArc", {"start": v(-3, -5.17) * mm, "mid": v(-2.7, -5.04) * mm, "end": v(-2.56, -4.72) * mm});
            skPoint(sketch, "E55.visualSharp", {"position": v(-3.76, -5.17) * mm});
            skArc(sketch, "E55.filletArc", {"start": v(-3.76, -4.72) * mm, "mid": v(-3.63, -5.04) * mm, "end": v(-3.3, -5.17) * mm});
            skPoint(sketch, "E56.visualSharp", {"position": v(-4.64, -5.17) * mm});
            skArc(sketch, "E56.filletArc", {"start": v(-5.09, -5.17) * mm, "mid": v(-4.77, -5.04) * mm, "end": v(-4.64, -4.72) * mm});
            skPoint(sketch, "E57.visualSharp", {"position": v(-5.84, -5.17) * mm});
            skArc(sketch, "E57.filletArc", {"start": v(-5.84, -4.72) * mm, "mid": v(-5.7, -5.04) * mm, "end": v(-5.39, -5.17) * mm});
            skPoint(sketch, "E58.visualSharp", {"position": v(-6.72, -5.17) * mm});
            skArc(sketch, "E58.filletArc", {"start": v(-7.17, -5.17) * mm, "mid": v(-6.85, -5.04) * mm, "end": v(-6.72, -4.72) * mm});
            skPoint(sketch, "E59.visualSharp", {"position": v(-8.8, -5.17) * mm});
            skArc(sketch, "E59.filletArc", {"start": v(-9.25, -5.17) * mm, "mid": v(-8.93, -5.04) * mm, "end": v(-8.8, -4.72) * mm});
            skPoint(sketch, "E60.visualSharp", {"position": v(-7.92, -5.17) * mm});
            skArc(sketch, "E60.filletArc", {"start": v(-7.92, -4.72) * mm, "mid": v(-7.79, -5.04) * mm, "end": v(-7.47, -5.17) * mm});
            skPoint(sketch, "E61.visualSharp", {"position": v(-10, -5.17) * mm});
            skArc(sketch, "E61.filletArc", {"start": v(-10, -4.72) * mm, "mid": v(-9.87, -5.04) * mm, "end": v(-9.55, -5.17) * mm});
            skLineSegment(sketch, "E62.bottom", {"start": v(-10.88, -4.42) * mm, "end": v(-12.08, -4.42) * mm});
            skLineSegment(sketch, "E62.top", {"start": v(-11.33, -5.17) * mm, "end": v(-11.63, -5.17) * mm});
            skLineSegment(sketch, "E62.left", {"start": v(-10.88, -4.42) * mm, "end": v(-10.88, -4.72) * mm});
            skLineSegment(sketch, "E62.right", {"start": v(-12.08, -4.42) * mm, "end": v(-12.08, -4.72) * mm});
            skPoint(sketch, "E63.visualSharp", {"position": v(-10.88, -5.17) * mm});
            skArc(sketch, "E63.filletArc", {"start": v(-11.33, -5.17) * mm, "mid": v(-11.01, -5.04) * mm, "end": v(-10.88, -4.72) * mm});
            skPoint(sketch, "E64.visualSharp", {"position": v(-12.08, -5.17) * mm});
            skArc(sketch, "E64.filletArc", {"start": v(-12.08, -4.72) * mm, "mid": v(-11.95, -5.04) * mm, "end": v(-11.63, -5.17) * mm});
            skLineSegment(sketch, "E65.bottom", {"start": v(-12.08, -4.42) * mm, "end": v(-12, -4.42) * mm});
            skLineSegment(sketch, "E65.top", {"start": v(-12.08, 0.58) * mm, "end": v(-12, 0.58) * mm});
            skLineSegment(sketch, "E65.left", {"start": v(-12.08, -4.42) * mm, "end": v(-12.08, 0.58) * mm});
            skLineSegment(sketch, "E65.right", {"start": v(-12, -4.42) * mm, "end": v(-12, 0.58) * mm});
            skLineSegment(sketch, "E66.bottom", {"start": v(1.68, -12) * mm, "end": v(-1.68, -12) * mm});
            skLineSegment(sketch, "E66.top", {"start": v(1.68, -6) * mm, "end": v(-1.68, -6) * mm});
            skLineSegment(sketch, "E66.left", {"start": v(1.68, -12) * mm, "end": v(1.68, -6) * mm});
            skLineSegment(sketch, "E66.right", {"start": v(-1.68, -12) * mm, "end": v(-1.68, -6) * mm});
            skSolve(sketch);
        }
        {
            var Q0;
            Q0=makeQuery(id+"F32.imprint","IMPRINT",FACE,{"disambiguationData":[TD([[makeQuery(id+"F32.imprint","IMPRINT",EDGE,{"derivedFrom":sQuery(id+"F32.wireOp",EDGE,"E27.bottom")}),1.0]])]});
            var Q1;
            Q1=makeQuery(id+"F32.imprint","IMPRINT",FACE,{"disambiguationData":[TD([[makeQuery(id+"F32.imprint","IMPRINT",EDGE,{"derivedFrom":sQuery(id+"F32.wireOp",EDGE,"E26.bottom")}),1.0]])]});
            var Q2;
            Q2=makeQuery(id+"F32.imprint","IMPRINT",FACE,{"disambiguationData":[TD([[makeQuery(id+"F32.imprint","IMPRINT",EDGE,{"derivedFrom":sQuery(id+"F32.wireOp",EDGE,"E29.top")}),-1.0]])]});
            var Q3;
            Q3=makeQuery(id+"F32.imprint","IMPRINT",FACE,{"disambiguationData":[TD([[makeQuery(id+"F32.imprint","IMPRINT",EDGE,{"derivedFrom":sQuery(id+"F32.wireOp",EDGE,"E28")}),-1.0]])]});
            var Q4;
            {var subQ1=sQuery(id+"F32.wireOp",EDGE,"E30.left");Q4=makeQuery(id+"F32.imprint","IMPRINT",FACE,{"disambiguationData":[TD([[makeQuery(id+"F32.imprint","IMPRINT",EDGE,{"derivedFrom":subQ1}),-1.0]])]});}
            var Q5;
            {var subQ1=sQuery(id+"F32.wireOp",EDGE,"E31.2.0.0");Q5=makeQuery(id+"F32.imprint","IMPRINT",FACE,{"disambiguationData":[TD([[makeQuery(id+"F32.imprint","IMPRINT",EDGE,{"derivedFrom":subQ1}),-1.0]])]});}
            var Q6;
            {var subQ1=sQuery(id+"F32.wireOp",EDGE,"E31.3.0.0");Q6=makeQuery(id+"F32.imprint","IMPRINT",FACE,{"disambiguationData":[TD([[makeQuery(id+"F32.imprint","IMPRINT",EDGE,{"derivedFrom":subQ1}),-1.0]])]});}
            var Q7;
            {var subQ1=sQuery(id+"F32.wireOp",EDGE,"E31.4.0.0");Q7=makeQuery(id+"F32.imprint","IMPRINT",FACE,{"disambiguationData":[TD([[makeQuery(id+"F32.imprint","IMPRINT",EDGE,{"derivedFrom":subQ1}),-1.0]])]});}
            var Q8;
            {var subQ0=sQuery(id+"F32.wireOp",EDGE,"E31.5.0.0");Q8=makeQuery(id+"F32.imprint","IMPRINT",FACE,{"disambiguationData":[TD([[makeQuery(id+"F32.imprint","IMPRINT",EDGE,{"derivedFrom":subQ0}),-1.0]])]});}
            var Q9;
            {var subQ1=sQuery(id+"F32.wireOp",EDGE,"E31.6.0.0");Q9=makeQuery(id+"F32.imprint","IMPRINT",FACE,{"disambiguationData":[TD([[makeQuery(id+"F32.imprint","IMPRINT",EDGE,{"derivedFrom":subQ1}),-1.0]])]});}
            var Q10;
            {var subQ0=sQuery(id+"F32.wireOp",EDGE,"E31.7.0.0");Q10=makeQuery(id+"F32.imprint","IMPRINT",FACE,{"disambiguationData":[TD([[makeQuery(id+"F32.imprint","IMPRINT",EDGE,{"derivedFrom":subQ0}),-1.0]])]});}
            var Q11;
            Q11=makeQuery(id+"F32.imprint","IMPRINT",FACE,{"disambiguationData":[TD([[makeQuery(id+"F32.imprint","IMPRINT",EDGE,{"derivedFrom":sQuery(id+"F32.wireOp",EDGE,"E65.bottom")}),1.0]])]});
            var Q12;
            {var subQ1=sQuery(id+"F32.wireOp",EDGE,"E31.8.0.0");Q12=makeQuery(id+"F32.imprint","IMPRINT",FACE,{"disambiguationData":[TD([[makeQuery(id+"F32.imprint","IMPRINT",EDGE,{"derivedFrom":subQ1}),-1.0]])]});}
            var Q13;
            {var subQ0=sQuery(id+"F32.wireOp",EDGE,"E31.9.0.0");Q13=makeQuery(id+"F32.imprint","IMPRINT",FACE,{"disambiguationData":[TD([[makeQuery(id+"F32.imprint","IMPRINT",EDGE,{"derivedFrom":subQ0}),-1.0]])]});}
            var Q14;
            Q14=makeQuery(id+"F32.imprint","IMPRINT",FACE,{"disambiguationData":[TD([[makeQuery(id+"F32.imprint","IMPRINT",EDGE,{"derivedFrom":sQuery(id+"F32.wireOp",EDGE,"E65.top")}),-1.0]])]});
            var Q15;
            Q15=makeQuery(id+"F32.imprint","IMPRINT",FACE,{"disambiguationData":[TD([[makeQuery(id+"F32.imprint","IMPRINT",EDGE,{"derivedFrom":sQuery(id+"F32.wireOp",EDGE,"E62.top")}),-1.0]])]});
            extrude(context, id + "F33", {"entities" : qUnion([Q0, Q1, Q2, Q3, Q4, Q5, Q6, Q7, Q8, Q9, Q10, Q11, Q12, Q13, Q14, Q15]), "operationType" : NewBodyOperationType.ADD, "oppositeDirection" : true, "depth" : 6 * mm});
        }
        {
            var Q0;
            Q0=makeQuery(id+"F33.opExtrude","CAP_EDGE",EDGE,{"disambiguationData":[OSD([sQuery(id+"F32.wireOp",EDGE,"E26.bottom")])],"isStart":false});
            var Q1;
            Q1=makeQuery(id+"F33.opExtrude","CAP_EDGE",EDGE,{"disambiguationData":[OSD([sQuery(id+"F32.wireOp",EDGE,"E27.bottom"),sQuery(id+"F32.wireOp",EDGE,"E65.top")])],"isStart":false});
            fillet(context, id + "F34", {"entities" : qUnion([Q0, Q1]), "radius" : 1.5 * mm, "tangentPropagation" : true, "allowEdgeOverflow" : false});
        }
    });
